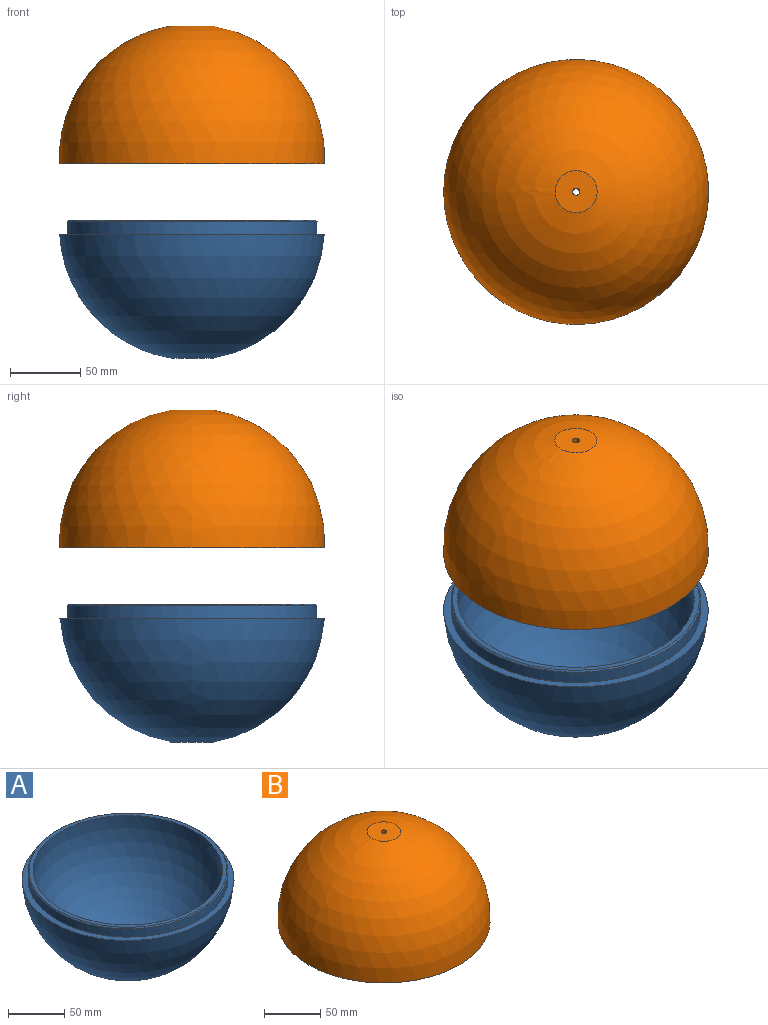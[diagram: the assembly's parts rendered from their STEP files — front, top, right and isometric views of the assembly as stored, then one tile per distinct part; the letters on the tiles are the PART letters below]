
ASSEMBLY  parts=2 mates=1
PART A: 8 faces, bbox 188.7x188.7x98.3 mm
  f0: sphere r=84.5mm, area 47497.7mm2, adj f1,f7
  f1: plane 176x176mm, normal (0,0,1), area 1975.3mm2, adj f0,f6
  f2: cylinder r=89mm len=178mm, axis (0,0,-1), area 5032.8mm2, adj f3,f6
  f3: plane 188.74x188.74mm, normal (0,0,1), area 3092.1mm2, adj f2,f4
  f4: sphere r=94.5mm, area 52430.2mm2, adj f3,f5
  f5: plane 30x30mm, normal (0,0,-1), area 686.4mm2, adj f4,f7
  f6: cone r=89mm half-angle=45deg, axis (0,0,-1), area 786.4mm2, adj f1,f2
  f7: cylinder r=2.55mm len=8.84mm, axis (0,0,-1), area 141.8mm2, adj f0,f5
PART B: 8 faces, bbox 189x189x98.3 mm
  f0: sphere r=84.5mm, area 42188.4mm2, adj f2,f7
  f1: cylinder r=90mm len=180mm, axis (0,0,-1), area 5089.4mm2, adj f2,f6
  f2: plane 180x180mm, normal (0,0,-1), area 3093.7mm2, adj f0,f1
  f3: plane 30x30mm, normal (0,0,1), area 686.4mm2, adj f4,f7
  f4: sphere r=94.5mm, area 58367.9mm2, adj f3,f5
  f5: plane 188.74x188.74mm, normal (0,0,-1), area 1961.1mm2, adj f4,f6
  f6: cone r=90mm half-angle=45deg, axis (0,0,-1), area 804.2mm2, adj f1,f5
  f7: cylinder r=2.55mm len=8.84mm, axis (0,0,1), area 141.8mm2, adj f0,f3
PLACE A t=(0,0,-50)mm
PLACE B at identity
MATE revolute A.f2 <-> B.f7  axis (0,0,1) through (0,0,-50)mm
